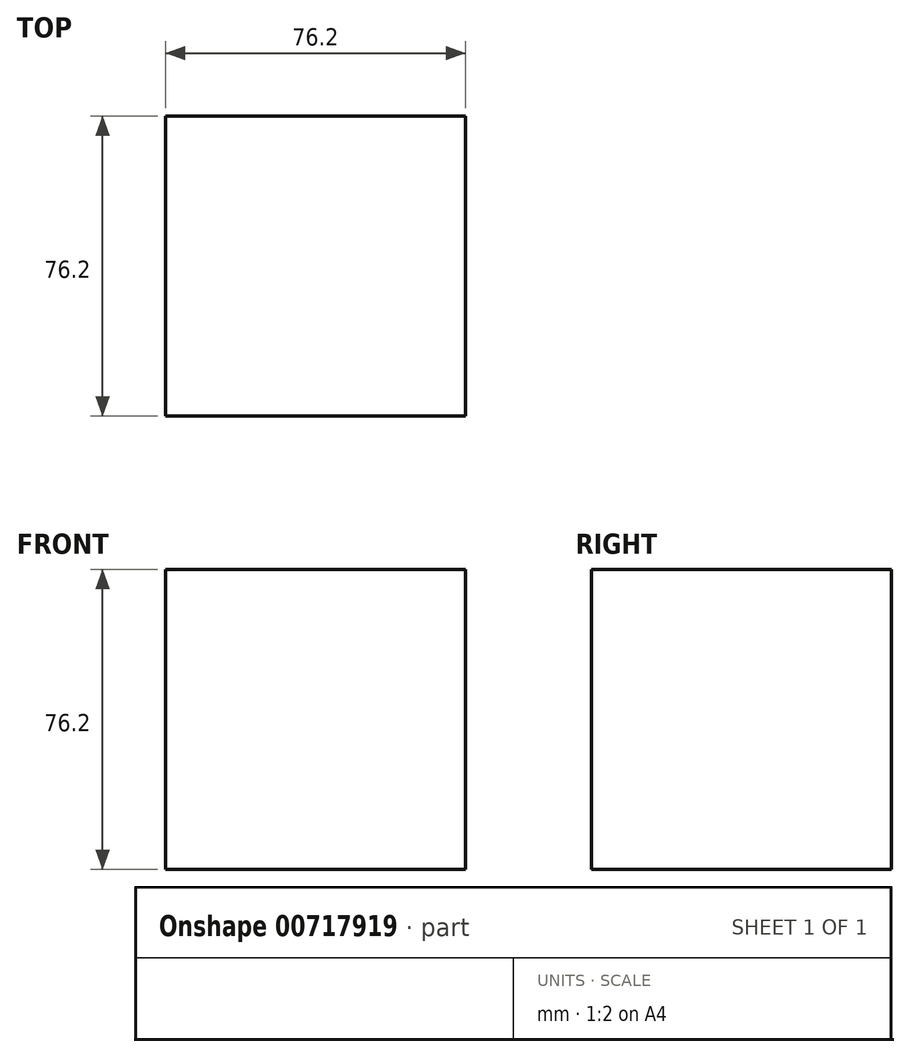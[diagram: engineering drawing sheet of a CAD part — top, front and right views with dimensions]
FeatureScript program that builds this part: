
annotation { "Feature Type Name" : "Feature", "Feature Type Description" : "" }
export const myFeature = defineFeature(function(context is Context, id is Id, definition is map)
    precondition{}
    {
        {
            var Q0;
            Q0=qCreatedBy(makeId("Front.planeOp"),FACE);
            var sketch = newSketch(context, id + "F0", { "sketchPlane" : qUnion([Q0])});
            skLineSegment(sketch, "E0.bottom", {"start": v(-36.43, 49.3) * mm, "end": v(39.77, 49.3) * mm});
            skLineSegment(sketch, "E0.top", {"start": v(-36.43, -26.9) * mm, "end": v(39.77, -26.9) * mm});
            skLineSegment(sketch, "E0.left", {"start": v(-36.43, 49.3) * mm, "end": v(-36.43, -26.9) * mm});
            skLineSegment(sketch, "E0.right", {"start": v(39.77, 49.3) * mm, "end": v(39.77, -26.9) * mm});
            skLineSegment(sketch, "E1.bottom", {"start": v(-43.19, 6.07) * mm, "end": v(-42.48, 6.07) * mm});
            skLineSegment(sketch, "E1.top", {"start": v(-43.19, 6.2) * mm, "end": v(-42.48, 6.2) * mm});
            skLineSegment(sketch, "E1.left", {"start": v(-43.19, 6.07) * mm, "end": v(-43.19, 6.2) * mm});
            skLineSegment(sketch, "E1.right", {"start": v(-42.48, 6.07) * mm, "end": v(-42.48, 6.2) * mm});
            skSolve(sketch);
        }
        {
            var Q0;
            Q0=makeQuery(id+"F0.imprint","IMPRINT",FACE,{"disambiguationData":[TD([[makeQuery(id+"F0.imprint","IMPRINT",EDGE,{"derivedFrom":sQuery(id+"F0.wireOp",EDGE,"E0.bottom")}),-1.0]])]});
            extrude(context, id + "F1", {"entities" : qUnion([Q0]), "endBound" : BoundingType.SYMMETRIC, "depth" : 76.2 * mm, "offsetDistance" : 25.4 * mm});
        }
        {
            var Q0;
            Q0=makeQuery(id+"F1.opExtrude","SWEPT_FACE",FACE,{"disambiguationData":[OSD([sQuery(id+"F0.wireOp",EDGE,"E0.left")])]});
            var sketch = newSketch(context, id + "F2", { "sketchPlane" : qUnion([Q0])});
            skCircle(sketch, "E2", {"center": v(0, 14.99) * mm, "radius": 33.86 * mm});
            skSolve(sketch);
        }
        {
            var Q0;
            Q0=makeQuery(id+"F2.imprint","IMPRINT",FACE,{"disambiguationData":[TD([[makeQuery(id+"F2.imprint","IMPRINT",EDGE,{"derivedFrom":sQuery(id+"F2.wireOp",EDGE,"E2")}),1.0]])]});
            extrude(context, id + "F3", {"entities" : qUnion([Q0]), "operationType" : NewBodyOperationType.REMOVE, "endBound" : BoundingType.THROUGH_ALL, "depth" : 304.8 * mm, "offsetDistance" : 25.4 * mm});
        }
    });
